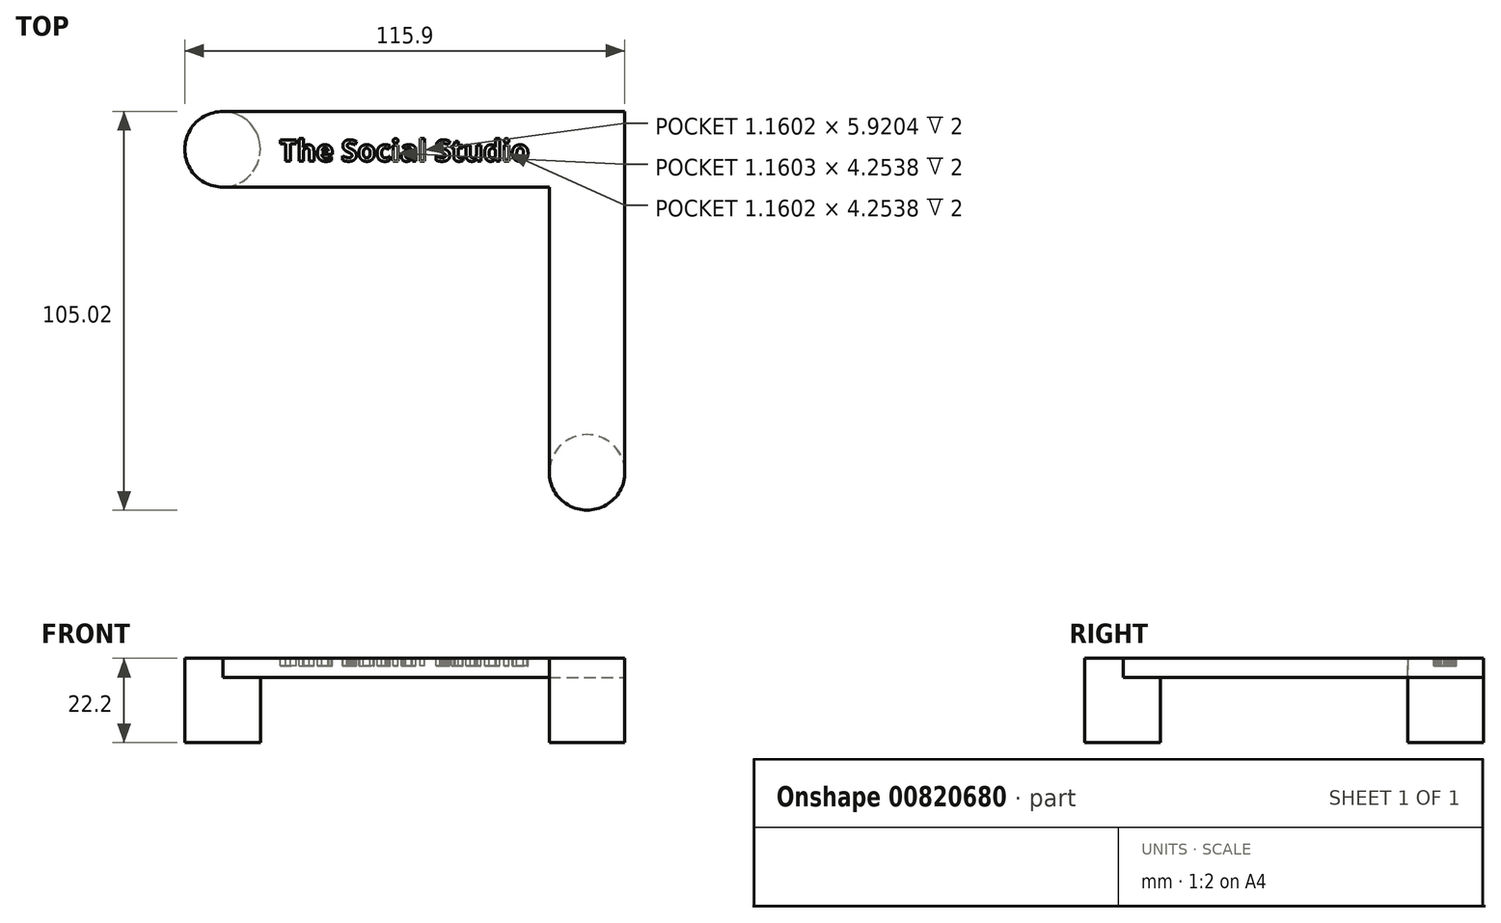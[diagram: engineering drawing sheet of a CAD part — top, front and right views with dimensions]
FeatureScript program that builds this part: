
annotation { "Feature Type Name" : "Feature", "Feature Type Description" : "" }
export const myFeature = defineFeature(function(context is Context, id is Id, definition is map)
    precondition{}
    {
        {
            var Q0;
            Q0=qCreatedBy(makeId("Top.planeOp"),FACE);
            var sketch = newSketch(context, id + "F0", { "sketchPlane" : qUnion([Q0])});
            skCircle(sketch, "E0", {"center": v(-48, 0) * mm, "radius": 9.95 * mm});
            skCircle(sketch, "E1.MirrorC", {"center": v(48, 0) * mm, "radius": 9.95 * mm});
            skLineSegment(sketch, "E2", {"start": v(47.8, 9.95) * mm, "end": v(48, -9.95) * mm, "construction": true});
            skLineSegment(sketch, "E3", {"start": v(-48.1, 9.95) * mm, "end": v(-48.1, -9.95) * mm, "construction": true});
            skSolve(sketch);
        }
        {
            var Q0;
            Q0=makeQuery(id+"F0.imprint","IMPRINT",FACE,{"disambiguationData":[TD([[makeQuery(id+"F0.imprint","IMPRINT",EDGE,{"derivedFrom":sQuery(id+"F0.wireOp",EDGE,"E0")}),1.0]])]});
            var Q1;
            Q1=makeQuery(id+"F0.imprint","IMPRINT",FACE,{"disambiguationData":[TD([[makeQuery(id+"F0.imprint","IMPRINT",EDGE,{"derivedFrom":sQuery(id+"F0.wireOp",EDGE,"E1.MirrorC")}),-1.0]])]});
            extrude(context, id + "F1", {"entities" : qUnion([Q0, Q1]), "depth" : 17.2 * mm, "offsetDistance" : 25 * mm});
        }
        {
            var Q0;
            Q0=makeQuery(id+"F1.opExtrude","CAP_FACE",FACE,{"disambiguationData":[OSD([sQuery(id+"F0.wireOp",EDGE,"E0")])],"isStart":false});
            var sketch = newSketch(context, id + "F2", { "sketchPlane" : qUnion([Q0])});
            skLineSegment(sketch, "E4.bottom", {"start": v(-48.16, -9.95) * mm, "end": v(48.16, -9.95) * mm});
            skLineSegment(sketch, "E4.top", {"start": v(-48.16, 9.95) * mm, "end": v(48.16, 9.95) * mm});
            skLineSegment(sketch, "E4.left", {"start": v(-48.16, -9.95) * mm, "end": v(-48.16, 9.95) * mm});
            skLineSegment(sketch, "E4.right", {"start": v(48.16, -9.95) * mm, "end": v(48.16, 9.95) * mm});
            skPoint(sketch, "E4.middle", {"position": v(0, 0) * mm});
            skSolve(sketch);
        }
        {
            var Q0;
            {var subQ0=sQuery(id+"F2.wireOp",EDGE,"E4.left");Q0=makeQuery(id+"F2.imprint","IMPRINT",FACE,{"disambiguationData":[TD([[makeQuery(id+"F2.imprint","IMPRINT",EDGE,{"derivedFrom":subQ0}),1.0]])]});}
            var Q1;
            {var subQ0=sQuery(id+"F2.wireOp",EDGE,"E4.right");Q1=makeQuery(id+"F2.imprint","IMPRINT",FACE,{"disambiguationData":[TD([[makeQuery(id+"F2.imprint","IMPRINT",EDGE,{"derivedFrom":subQ0}),1.0]])]});}
            var Q2;
            {var subQ0=sQuery(id+"F2.wireOp",EDGE,"E4.left");Q2=makeQuery(id+"F2.imprint","IMPRINT",FACE,{"disambiguationData":[TD([[makeQuery(id+"F2.imprint","IMPRINT",EDGE,{"derivedFrom":subQ0}),-1.0]])]});}
            var Q3;
            Q3=makeQuery(id+"F1.opExtrude","CAP_FACE",FACE,{"disambiguationData":[OSD([sQuery(id+"F0.wireOp",EDGE,"E1.MirrorC")])],"isStart":false});
            var Q4;
            Q4=makeQuery(id+"F1.opExtrude","CAP_FACE",FACE,{"disambiguationData":[OSD([sQuery(id+"F0.wireOp",EDGE,"E0")])],"isStart":false});
            var Q5;
            Q5=makeQuery(id+"F1.opExtrude","CAP_FACE",FACE,{"disambiguationData":[OSD([sQuery(id+"F0.wireOp",EDGE,"E1.MirrorC")])],"isStart":true});
            var Q6;
            Q6=makeQuery(id+"F1.opExtrude","CAP_FACE",FACE,{"disambiguationData":[OSD([sQuery(id+"F0.wireOp",EDGE,"E0")])],"isStart":true});
            var Q7;
            {var subQ0=sQuery(id+"F2.wireOp",EDGE,"E4.top");var subQ1=makeQuery(id+"F1.opExtrude","CAP_EDGE",EDGE,{"disambiguationData":[OSD([sQuery(id+"F0.wireOp",EDGE,"E0")])],"isStart":false});var subQ3=makeQuery(id+"F2.imprint","INTERSECT",VERTEX,{"derivedFrom":[subQ1,subQ0]});Q7=makeQuery(id+"F2.imprint","IMPRINT",FACE,{"disambiguationData":[TD([[makeQuery(id+"F2.imprint","IMPRINT",EDGE,{"disambiguationData":[TD([[subQ3,1.0]])],"derivedFrom":subQ0}),1.0]])]});}
            var Q8;
            {var subQ0=sQuery(id+"F2.wireOp",EDGE,"E4.bottom");var subQ1=makeQuery(id+"F1.opExtrude","CAP_EDGE",EDGE,{"disambiguationData":[OSD([sQuery(id+"F0.wireOp",EDGE,"E0")])],"isStart":false});var subQ3=makeQuery(id+"F2.imprint","INTERSECT",VERTEX,{"derivedFrom":[subQ1,subQ0]});Q8=makeQuery(id+"F2.imprint","IMPRINT",FACE,{"disambiguationData":[TD([[makeQuery(id+"F2.imprint","IMPRINT",EDGE,{"disambiguationData":[TD([[subQ3,1.0]])],"derivedFrom":subQ0}),-1.0]])]});}
            extrude(context, id + "F3", {"entities" : qUnion([Q0, Q1, Q2, Q3, Q4, Q5, Q6, Q7, Q8]), "depth" : 5 * mm, "offsetDistance" : 25 * mm});
        }
        {
            var Q0;
            Q0=makeQuery(id+"F3.opExtrude","CAP_FACE",FACE,{"disambiguationData":[OSD([sQuery(id+"F0.wireOp",EDGE,"E0"),sQuery(id+"F2.wireOp",EDGE,"E4.bottom"),sQuery(id+"F2.wireOp",EDGE,"E4.top"),sQuery(id+"F2.wireOp",EDGE,"E4.right")])],"isStart":false});
            var sketch = newSketch(context, id + "F4", { "sketchPlane" : qUnion([Q0])});
            skText(sketch, "E5", { "text": "The Social Studio", "fontName": "OpenSans-Bold.ttf"});
            const initialGuessF4  = {"E5": [-0.033, -0.00312, 1, 0, 0.00561]};
            skSetInitialGuess(sketch, initialGuessF4);
            skSolve(sketch);
        }
        {
            var Q0;
            Q0=qSketchRegion(id+"F4",true);
            extrude(context, id + "F5", {"entities" : qUnion([Q0]), "operationType" : NewBodyOperationType.REMOVE, "oppositeDirection" : true, "depth" : 2 * mm, "offsetDistance" : 25 * mm});
        }
        {
            var Q0;
            {var subQ0=sQuery(id+"F0.wireOp",EDGE,"E1.MirrorC");Q0=makeQuery(id+"F3.opExtrude","SWEPT_BODY",BODY,{"disambiguationData":[OSD([subQ0]),TDD([makeQuery(id+"F1.opExtrude","CAP_FACE",FACE,{"disambiguationData":[OSD([subQ0])],"isStart":true})])]});}
            var Q1;
            {var subQ0=sQuery(id+"F0.wireOp",EDGE,"E0");Q1=makeQuery(id+"F3.opExtrude","SWEPT_BODY",BODY,{"disambiguationData":[OSD([subQ0]),TDD([makeQuery(id+"F1.opExtrude","CAP_FACE",FACE,{"disambiguationData":[OSD([subQ0])],"isStart":false})])]});}
            var Q2;
            {var subQ0=sQuery(id+"F0.wireOp",EDGE,"E0");Q2=makeQuery(id+"F3.opExtrude","SWEPT_BODY",BODY,{"disambiguationData":[OSD([subQ0]),TDD([makeQuery(id+"F1.opExtrude","CAP_FACE",FACE,{"disambiguationData":[OSD([subQ0])],"isStart":true})])]});}
            var Q3;
            Q3=makeQuery(id+"F1.opExtrude","SWEPT_BODY",BODY,{"disambiguationData":[OSD([sQuery(id+"F0.wireOp",EDGE,"E1.MirrorC")])]});
            var Q4;
            Q4=makeQuery(id+"F1.opExtrude","SWEPT_BODY",BODY,{"disambiguationData":[OSD([sQuery(id+"F0.wireOp",EDGE,"E0")])]});
            var Q5;
            {var subQ0=sQuery(id+"F0.wireOp",EDGE,"E1.MirrorC");Q5=makeQuery(id+"F3.opExtrude","SWEPT_BODY",BODY,{"disambiguationData":[OSD([subQ0]),TDD([makeQuery(id+"F1.opExtrude","CAP_FACE",FACE,{"disambiguationData":[OSD([subQ0])],"isStart":false})])]});}
            var Q6;
            Q6=makeQuery(id+"F3.opExtrude","SWEPT_BODY",BODY,{"disambiguationData":[OSD([sQuery(id+"F0.wireOp",EDGE,"E0"),sQuery(id+"F2.wireOp",EDGE,"E4.bottom"),sQuery(id+"F2.wireOp",EDGE,"E4.top"),sQuery(id+"F2.wireOp",EDGE,"E4.right")])]});
            booleanBodies(context, id + "F6", {"operationType" : BooleanOperationType.UNION, "tools" : qUnion([Q0, Q1, Q2, Q3, Q4, Q5, Q6])});
        }
        {
            var Q0;
            {var subQ0=sQuery(id+"F2.wireOp",EDGE,"E4.bottom");var subQ2=sQuery(id+"F2.wireOp",EDGE,"E4.top");var subQ3=sQuery(id+"F0.wireOp",EDGE,"E0");var subQ7=sQuery(id+"F2.wireOp",EDGE,"E4.right");var subQ8=sQuery(id+"F0.wireOp",EDGE,"E1.MirrorC");Q0=makeQuery(id+"F6.opBoolean","MERGE",FACE,{"derivedFrom":[makeQuery(id+"F3.opExtrude","CAP_FACE",FACE,{"disambiguationData":[OSD([subQ3]),TDD([makeQuery(id+"F1.opExtrude","CAP_FACE",FACE,{"disambiguationData":[OSD([subQ3])],"isStart":false})])],"isStart":false}),makeQuery(id+"F3.opExtrude","CAP_FACE",FACE,{"disambiguationData":[OSD([subQ8]),TDD([makeQuery(id+"F1.opExtrude","CAP_FACE",FACE,{"disambiguationData":[OSD([subQ8])],"isStart":false})])],"isStart":false}),makeQuery(id+"F5.boolean.opBoolean","SPLIT",FACE,{"disambiguationData":[TD([makeQuery(id+"F3.opExtrude","SWEPT_FACE",FACE,{"disambiguationData":[OSD([subQ0])]})])],"derivedFrom":makeQuery(id+"F3.opExtrude","CAP_FACE",FACE,{"disambiguationData":[OSD([subQ3,subQ0,subQ2,subQ7])],"isStart":false})})]});}
            var sketch = newSketch(context, id + "F7", { "sketchPlane" : qUnion([Q0])});
            skLineSegment(sketch, "E6.bottom", {"start": v(38.05, 9.95) * mm, "end": v(57.95, 9.95) * mm});
            skLineSegment(sketch, "E6.top", {"start": v(38.05, -85.12) * mm, "end": v(57.95, -85.12) * mm});
            skLineSegment(sketch, "E6.left", {"start": v(38.05, 9.95) * mm, "end": v(38.05, -85.12) * mm});
            skLineSegment(sketch, "E6.right", {"start": v(57.95, 9.95) * mm, "end": v(57.95, -85.12) * mm});
            skSolve(sketch);
        }
        {
            var Q0;
            {var subQ1=sQuery(id+"F7.wireOp",EDGE,"E6.top");Q0=makeQuery(id+"F7.imprint","IMPRINT",FACE,{"disambiguationData":[TD([[makeQuery(id+"F7.imprint","IMPRINT",EDGE,{"derivedFrom":subQ1}),1.0]])]});}
            extrude(context, id + "F8", {"entities" : qUnion([Q0]), "operationType" : NewBodyOperationType.ADD, "oppositeDirection" : true, "depth" : 5 * mm, "offsetDistance" : 25 * mm});
        }
        {
            var Q0;
            {var subQ0=sQuery(id+"F2.wireOp",EDGE,"E4.bottom");var subQ1=sQuery(id+"F0.wireOp",EDGE,"E1.MirrorC");Q0=makeQuery(id+"F8.boolean.opBoolean","MERGE",FACE,{"derivedFrom":[makeQuery(id+"F6.opBoolean","MERGE",FACE,{"derivedFrom":[makeQuery(id+"F3.opExtrude","CAP_FACE",FACE,{"disambiguationData":[OSD([subQ1]),TDD([makeQuery(id+"F1.opExtrude","CAP_FACE",FACE,{"disambiguationData":[OSD([subQ1])],"isStart":false})])],"isStart":true}),makeQuery(id+"F3.opExtrude","CAP_FACE",FACE,{"disambiguationData":[OSD([sQuery(id+"F0.wireOp",EDGE,"E0"),subQ0,sQuery(id+"F2.wireOp",EDGE,"E4.top"),sQuery(id+"F2.wireOp",EDGE,"E4.right")])],"isStart":true})]}),makeQuery(id+"F8.opExtrude","CAP_FACE",FACE,{"disambiguationData":[OSD([subQ1,subQ0,sQuery(id+"F7.wireOp",EDGE,"E6.bottom"),sQuery(id+"F7.wireOp",EDGE,"E6.top"),sQuery(id+"F7.wireOp",EDGE,"E6.left"),sQuery(id+"F7.wireOp",EDGE,"E6.right")])],"isStart":false})]});}
            var sketch = newSketch(context, id + "F9", { "sketchPlane" : qUnion([Q0])});
            skCircle(sketch, "E7", {"center": v(48, 85.12) * mm, "radius": 9.95 * mm});
            skSolve(sketch);
        }
        {
            var Q0;
            Q0 = qSketchRegion(id + "F9", true);
            extrude(context, id + "F10", {"entities" : qUnion([Q0]), "operationType" : NewBodyOperationType.ADD, "depth" : 17.2 * mm, "offsetDistance" : 25 * mm});
        }
        {
            var Q0;
            Q0=makeQuery(id+"F10.opExtrude","CAP_FACE",FACE,{"disambiguationData":[OSD([sQuery(id+"F9.wireOp",EDGE,"E7")])],"isStart":true});
            extrude(context, id + "F11", {"entities" : qUnion([Q0]), "operationType" : NewBodyOperationType.ADD, "depth" : 5 * mm, "offsetDistance" : 25 * mm});
        }
    });
